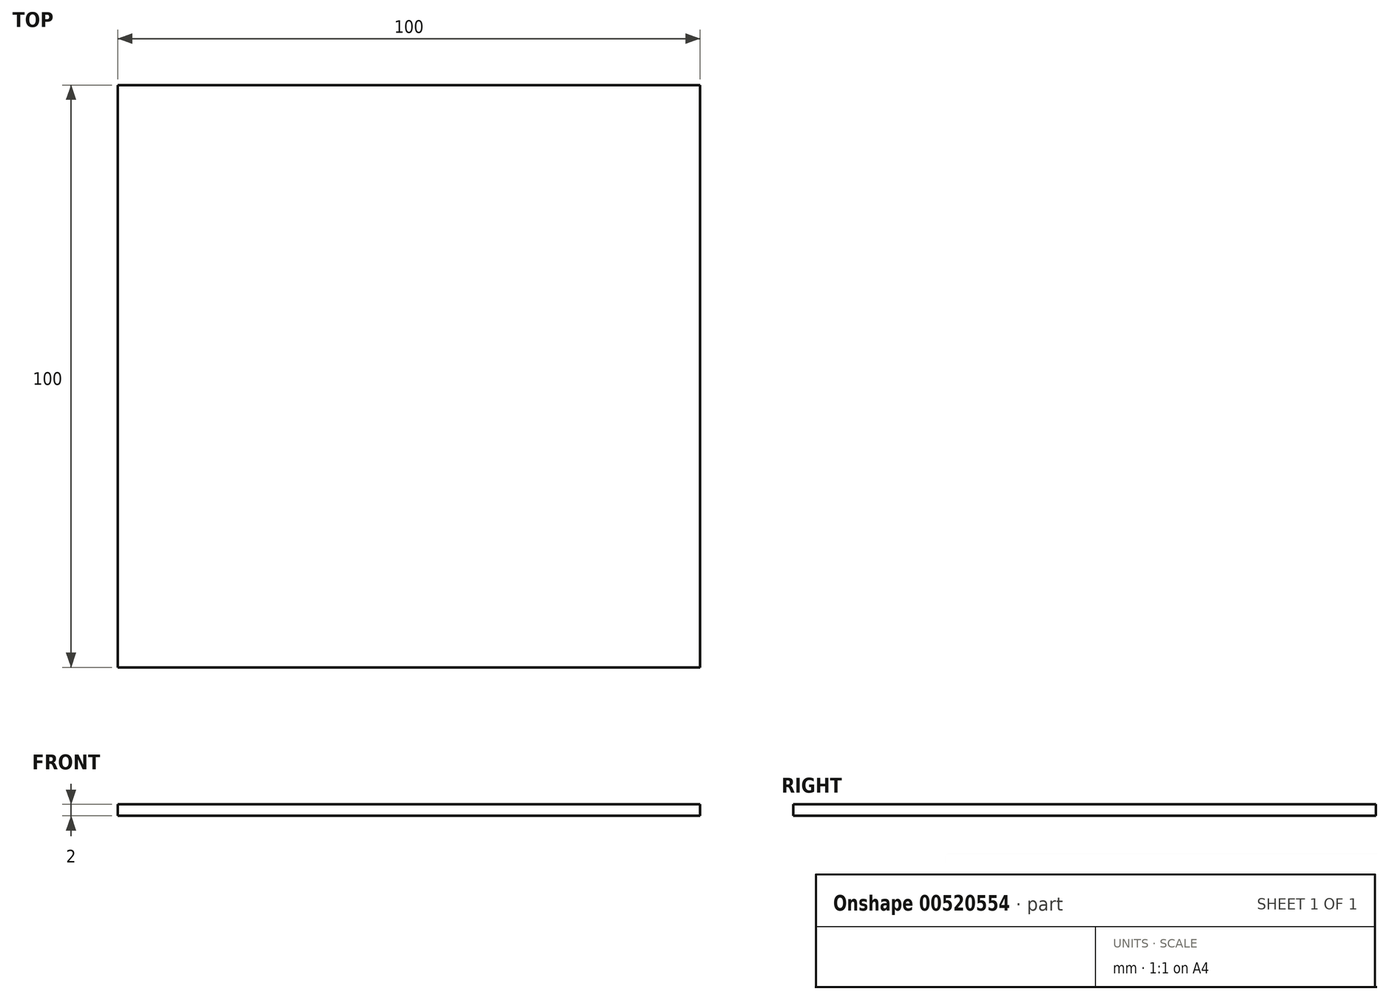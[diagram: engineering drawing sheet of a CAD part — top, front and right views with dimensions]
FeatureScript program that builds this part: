
annotation { "Feature Type Name" : "Feature", "Feature Type Description" : "" }
export const myFeature = defineFeature(function(context is Context, id is Id, definition is map)
    precondition{}
    {
        {
            var Q0;
            Q0=qCreatedBy(makeId("Top.planeOp"),FACE);
            var sketch = newSketch(context, id + "F0", { "sketchPlane" : qUnion([Q0])});
            skLineSegment(sketch, "E0.bottom", {"start": v(50, 50) * mm, "end": v(-50, 50) * mm});
            skLineSegment(sketch, "E0.top", {"start": v(50, -50) * mm, "end": v(-50, -50) * mm});
            skLineSegment(sketch, "E0.left", {"start": v(50, 50) * mm, "end": v(50, -50) * mm});
            skLineSegment(sketch, "E0.right", {"start": v(-50, 50) * mm, "end": v(-50, -50) * mm});
            skPoint(sketch, "E0.middle", {"position": v(0, 0) * mm});
            skSolve(sketch);
        }
        {
            var Q0;
            Q0 = qSketchRegion(id + "F0", true);
            extrude(context, id + "F1", {"entities" : qUnion([Q0]), "depth" : 2 * mm, "offsetDistance" : 25 * mm});
        }
    });
